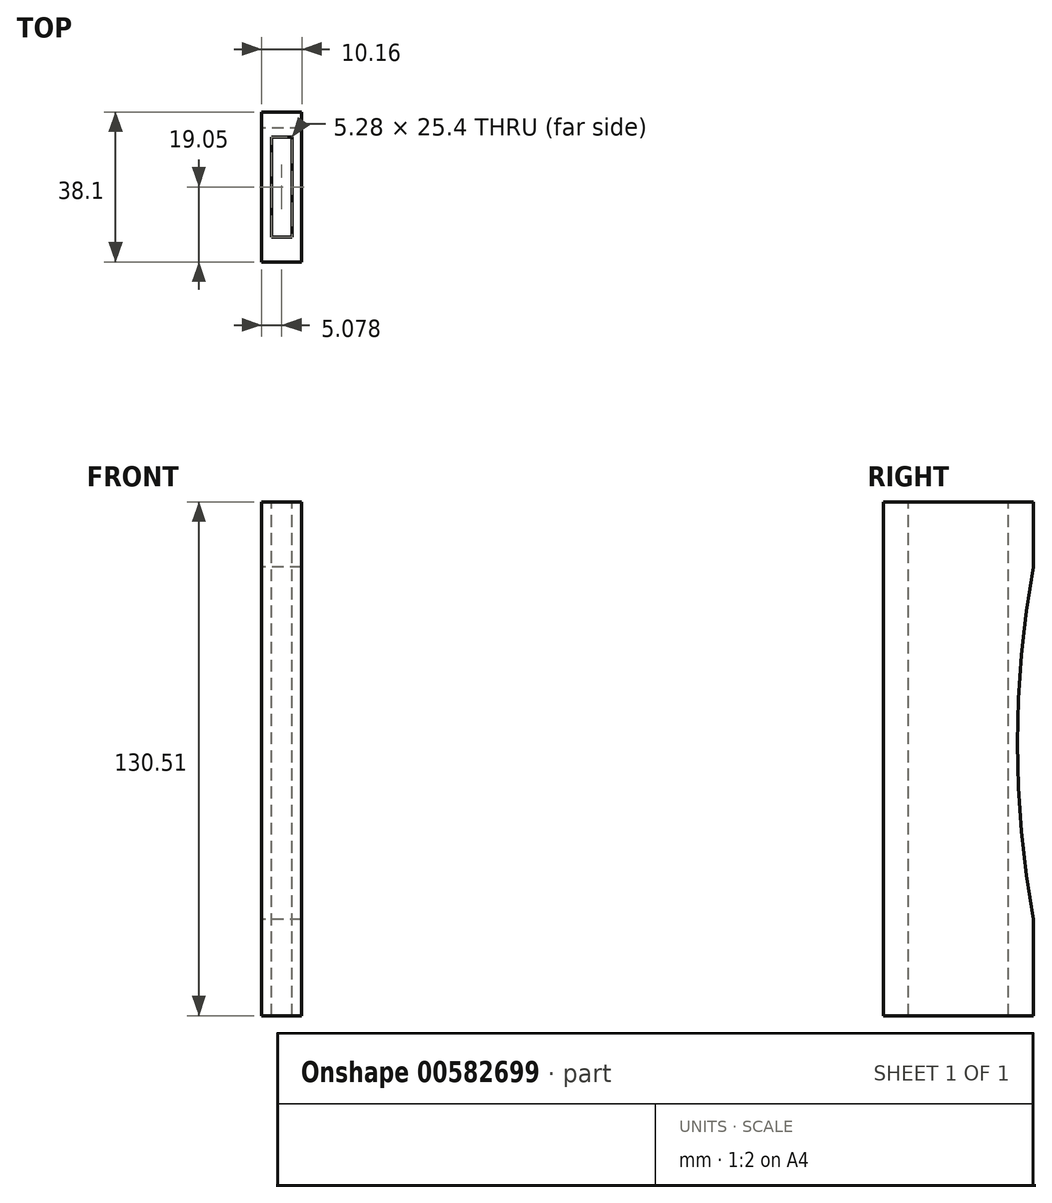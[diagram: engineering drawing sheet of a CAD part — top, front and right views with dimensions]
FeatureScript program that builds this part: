
annotation { "Feature Type Name" : "Feature", "Feature Type Description" : "" }
export const myFeature = defineFeature(function(context is Context, id is Id, definition is map)
    precondition{}
    {
        {
            var Q0;
            Q0=qCreatedBy(makeId("Front.planeOp"),FACE);
            var sketch = newSketch(context, id + "F0", { "sketchPlane" : qUnion([Q0])});
            skLineSegment(sketch, "E0", {"start": v(14.65, 52.8) * mm, "end": v(14.65, -77.7) * mm});
            skLineSegment(sketch, "E1", {"start": v(14.65, -77.7) * mm, "end": v(4.49, -77.7) * mm});
            skLineSegment(sketch, "E2", {"start": v(4.49, -77.7) * mm, "end": v(4.49, 52.8) * mm});
            skLineSegment(sketch, "E3", {"start": v(4.49, 52.8) * mm, "end": v(14.65, 52.8) * mm});
            skSolve(sketch);
        }
        {
            var Q0;
            Q0 = qSketchRegion(id + "F0", true);
            extrude(context, id + "F1", {"entities" : qUnion([Q0]), "depth" : 38.1 * mm, "offsetDistance" : 25.4 * mm});
        }
        {
            var Q0;
            Q0=makeQuery(id+"F1.opExtrude","SWEPT_FACE",FACE,{"disambiguationData":[OSD([sQuery(id+"F0.wireOp",EDGE,"E3")])]});
            var sketch = newSketch(context, id + "F2", { "sketchPlane" : qUnion([Q0])});
            skSolve(sketch);
        }
        {
            var Q0;
            {var subQ0=sQuery(id+"F0.wireOp",EDGE,"E3");Q0=makeQuery(id+"F2.imprint","IMPRINT",FACE,{"disambiguationData":[TD([[makeQuery(id+"F2.imprint","IMPRINT",EDGE,{"derivedFrom":makeQuery(id+"F1.opExtrude","CAP_EDGE",EDGE,{"disambiguationData":[OSD([subQ0])],"isStart":true})}),-1.0]])]});}
            var sketch = newSketch(context, id + "F3", { "sketchPlane" : qUnion([Q0])});
            skLineSegment(sketch, "E4.0", {"start": v(4.49, -38.1) * mm, "end": v(4.49, 0) * mm});
            skLineSegment(sketch, "E5.0", {"start": v(14.65, -38.1) * mm, "end": v(14.65, 0) * mm});
            skLineSegment(sketch, "E6", {"start": v(6.93, -31.75) * mm, "end": v(12.2, -31.75) * mm});
            skLineSegment(sketch, "E7", {"start": v(12.2, -31.75) * mm, "end": v(12.2, -6.35) * mm});
            skLineSegment(sketch, "E8", {"start": v(6.93, -31.75) * mm, "end": v(6.93, -6.35) * mm});
            skLineSegment(sketch, "E9", {"start": v(6.93, -6.35) * mm, "end": v(12.2, -6.35) * mm});
            skSolve(sketch);
        }
        {
            var Q0;
            Q0=makeQuery(id+"F1.opExtrude","SWEPT_FACE",FACE,{"disambiguationData":[OSD([sQuery(id+"F0.wireOp",EDGE,"E2")])]});
            var sketch = newSketch(context, id + "F4", { "sketchPlane" : qUnion([Q0])});
            skPoint(sketch, "E10", {"position": v(0, 26.13) * mm});
            skPoint(sketch, "E11", {"position": v(0, -53.21) * mm});
            skPoint(sketch, "E12", {"position": v(0, 36.3) * mm});
            skArc(sketch, "E13", {"start": v(0, -53.21) * mm, "mid": v(4.08, -8.45) * mm, "end": v(0, 36.3) * mm});
            skLineSegment(sketch, "E14", {"start": v(0, 36.3) * mm, "end": v(0, -53.21) * mm});
            skSolve(sketch);
        }
        {
            var Q0;
            Q0 = qSketchRegion(id + "F4", true);
            extrude(context, id + "F5", {"entities" : qUnion([Q0]), "operationType" : NewBodyOperationType.REMOVE, "oppositeDirection" : true, "depth" : 25.4 * mm, "offsetDistance" : 25.4 * mm});
        }
        {
            var Q0;
            Q0 = qSketchRegion(id + "F3", true);
            extrude(context, id + "F6", {"entities" : qUnion([Q0]), "operationType" : NewBodyOperationType.REMOVE, "oppositeDirection" : true, "depth" : 152.4 * mm, "offsetDistance" : 25.4 * mm});
        }
    });
